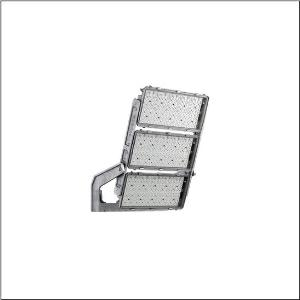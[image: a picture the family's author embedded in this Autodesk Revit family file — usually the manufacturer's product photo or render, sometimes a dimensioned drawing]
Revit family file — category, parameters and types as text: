
# Revit family: floodlight_fl_11_maxi_pro_remote___pl43_5xa779425a01aa_2185
name_source: partatom
category: Lighting Fixtures
units: mm (PartAtom-declared; Revit-internal decimal feet)

## family parameters
Cut with Voids When Loaded = No
Host = Face
Light Source = No
Part Type = Normal
Room Calculation Point = No
Round Connector Dimension = Use Diameter
Shared = No

## types (1)
- --- (1 x LED, 162210 lm, 1334.7 W, 3000K)
    Apparent Load = 1335 VA
    CIE Flux Codes = 25 74 99 100 100
    Color Rendering = 70
    Color Temperature = 3000K
    Default Elevation = 1800 mm
    Description = Floodlight FL 11  maxi  pro Remote floodlight; light control with lens of PMMA; cover panel of toughened safety glass, transparent; light distribution: PL43, asymmetric direct distribution, LEDcolour temperature: 3000K, rated luminous flux: 162.210lm, colour rendering: CRI > 70, light colour: 730; luminous efficacy: 122lm/W; brightness control: DALI 2 (1 DALI address); with terminal, 8-pole, max. 2.5mm², mains connection: 220..240V/380..400V AC, 50/60Hz, surge voltage resistance: line to ground: 10kV, ECG replaceable separately, LED unit replaceable without ESD environment, dustproof LED module, dimming range 10..100%, no afterglow with DALI off / DMX off command; 1335W floodlight with 2x LED unit of diecast aluminium, coated grey; length: 713mm / width: 651mm / height: 338mm; mounting bracket, of diecast aluminium, uncoated, natural, equipment: Power, protection rating (complete): IP66; insulation class (complete): insulation class I (protective earthing); certification: CE, ENEC, VDE; ball protection: ball impact resistance with accessories, impact resistance: IK07; rated ambient temperature 10°C, only for outdoor installations, permissible operating ambient temperature: -40..+30°C, permissible storage temperature: -40..+85°C; packaging unit: 1 piece

Light Distribution: PL43
    Height = 320 mm
    Lamp = 1 x LED
    Lamp Light Flux = 162210 lm
    Lamp Power = 1334.7 W
    Lamp count = 1
    Length = 1002 mm
    Luminous efficacy = 122 lm/W
    Manufacturer = Siteco
    ModVariant = No
    Model = 5XA779425A01AA
    Mounting Place = Ceiling
    Mounting Type = Surface mounted
    Number of Poles = 1
    OnlyDefault = Yes
    Power Factor = 1
    Product Name = Floodlight FL 11 maxi pro Remote | PL43
    Product group = floodlight | ceiling mounted
    ProductGroupID = 302
    Protection Class = Protection class I
    Protection Degree = IP 66
    RLX_Detail_Level = 1
    RLX_Emergency_Light_Flux = 0 lm
    RLX_Emergency_Type = 0
    RLX_Emergency_Type_DB = No
    RlxData = <blob elided: 52477 chars, md5=19d3d66c>
    Socket = socket
    Standby Power = 0 W
    System Light Flux = 162210 lm
    System Power = 1335 W
    Type Comments = factory setting: luminous flux: 100 % | dim-lin: 254 | 920 mA
    Type Image = l_1006784.jpg
    URL = http://relux.com
    VarID = @adj_065107
    Voltage = 0 V
    Weight = 0.00 kg
    Width = 655 mm

## geometry (parser evidence)
native form markers: Blend x4, Sweep x13
no freeform markers — native parametric forms only
